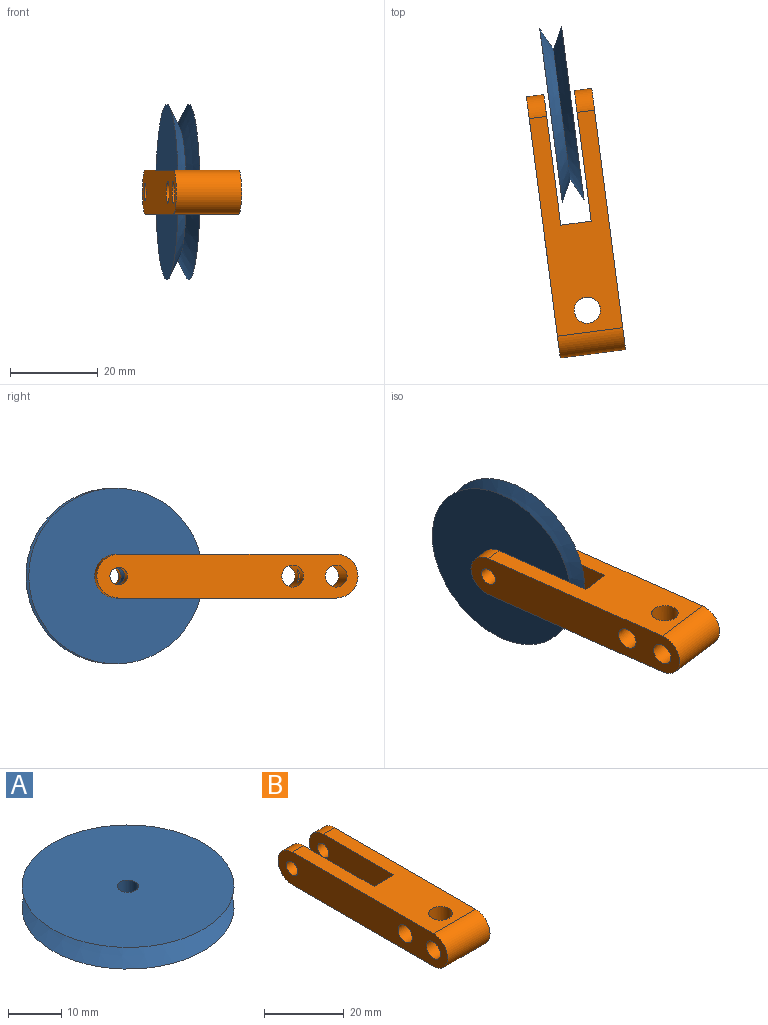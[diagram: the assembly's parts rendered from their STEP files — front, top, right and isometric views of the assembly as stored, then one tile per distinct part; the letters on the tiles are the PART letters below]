
ASSEMBLY  parts=2 mates=1
PART A: 5 faces, bbox 40x40x5 mm
  f0: plane 40x40mm, normal (0,0,-1), area 1244.1mm2, adj f3,f4
  f1: plane 40x40mm, normal (0,0,1), area 1244.1mm2, adj f2,f4
  f2: cone r=20mm half-angle=63.4deg, axis (0,0,1), area 614.7mm2, adj f1,f3
  f3: cone r=15mm half-angle=63.4deg, axis (0,0,-1), area 614.7mm2, adj f0,f2
  f4: cylinder r=2mm len=5mm, axis (0,0,-1), area 62.8mm2, adj f0,f1
PART B: 15 faces, bbox 15x60x10 mm
  f0: plane 60x10mm, normal (-1,0,0), area 526.7mm2, adj f5,f6,f7,f10,f11,f12,f13
  f1: plane 60x10mm, normal (1,0,0), area 526.7mm2, adj f5,f6,f8,f9,f10,f12,f13
  f2: plane 30x10mm, normal (-1,0,0), area 276.7mm2, adj f3,f5,f6,f8,f9
  f3: plane 10x7mm, normal (0,1,0), area 70mm2, adj f2,f4,f5,f6
  f4: plane 30x10mm, normal (1,0,0), area 276.7mm2, adj f3,f5,f6,f7,f11
  f5: plane 50x15mm, normal (0,0,1), area 546.7mm2, adj f0,f1,f2,f3,f4,f9,f10,f11
  f6: plane 50x15mm, normal (0,0,-1), area 546.7mm2, adj f0,f1,f2,f3,f4,f9,f10,f11
  f7: cylinder r=2mm len=4mm, axis (-1,0,0), area 50.3mm2, adj f0,f4
  f8: cylinder r=2mm len=4mm, axis (-1,0,0), area 50.3mm2, adj f1,f2
  f9: cylinder r=5mm len=10mm, axis (1,0,0), area 62.8mm2, adj f1,f2,f5,f6
  f10: cylinder r=5mm len=15mm, axis (-1,0,0), area 235.6mm2, adj f0,f1,f5,f6
  f11: cylinder r=5mm len=10mm, axis (1,0,0), area 62.8mm2, adj f0,f4,f5,f6
  f12: cylinder r=2.5mm len=15mm, axis (1,0,0), area 227.2mm2, adj f0,f1,f14
  f13: cylinder r=2.5mm len=15mm, axis (1,0,0), area 227.2mm2, adj f0,f1,f14
  f14: cylinder r=3mm len=10mm, axis (0,0,-1), area 171.8mm2, adj f5,f6,f12,f13
PLACE A rot(axis=(-0.06,1,0.06),90.2deg) t=(38.19,38.72,6.7)mm
PLACE B rot(axis=(0,0,1),7.4deg) t=(41.41,13.93,1.7)mm
MATE fastened A.f4 <-> B.f11  axis (-0.99,-0.13,0) through (40.67,39.04,6.7)mm
